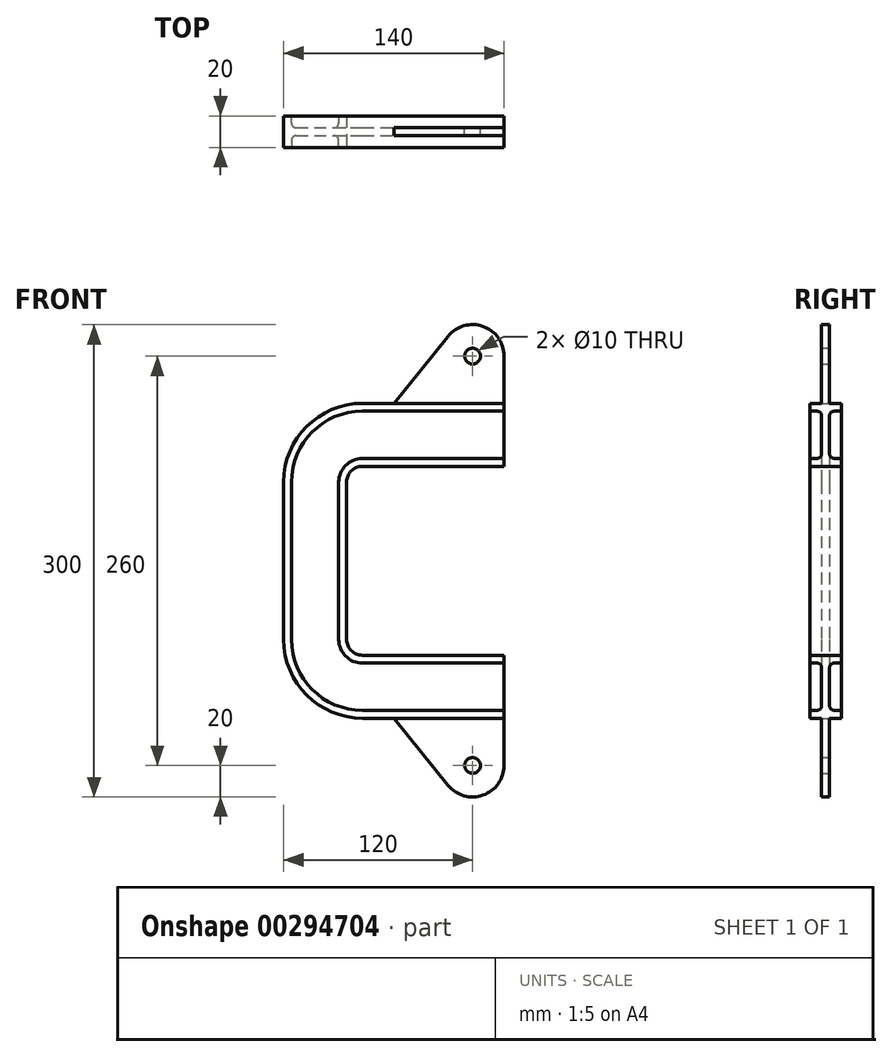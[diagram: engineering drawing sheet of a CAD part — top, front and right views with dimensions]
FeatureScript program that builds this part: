
annotation { "Feature Type Name" : "Feature", "Feature Type Description" : "" }
export const myFeature = defineFeature(function(context is Context, id is Id, definition is map)
    precondition{}
    {
        {
            var Q0;
            Q0=qCreatedBy(makeId("Front.planeOp"),FACE);
            var sketch = newSketch(context, id + "F0", { "sketchPlane" : qUnion([Q0])});
            skLineSegment(sketch, "E0", {"start": v(-100, 50) * mm, "end": v(-100, 0) * mm});
            skArc(sketch, "E1", {"start": v(-90, 60) * mm, "mid": v(-97.07, 57.07) * mm, "end": v(-100, 50) * mm});
            skLineSegment(sketch, "E2", {"start": v(-90, 60) * mm, "end": v(0, 60) * mm});
            skArc(sketch, "E3.MirrorCS", {"start": v(-90, -60) * mm, "mid": v(-97.07, -57.07) * mm, "end": v(-100, -50) * mm});
            skLineSegment(sketch, "E4.MirrorCS", {"start": v(-100, -50) * mm, "end": v(-100, 0) * mm});
            skLineSegment(sketch, "E5.MirrorCS", {"start": v(-90, -60) * mm, "end": v(0, -60) * mm});
            skSolve(sketch);
        }
        {
            var Q0;
            Q0=qCreatedBy(makeId("Right.planeOp"),FACE);
            var sketch = newSketch(context, id + "F1", { "sketchPlane" : qUnion([Q0])});
            skLineSegment(sketch, "E6", {"start": v(0, 60) * mm, "end": v(-10, 60) * mm});
            skLineSegment(sketch, "E7", {"start": v(-10, 60) * mm, "end": v(-10, 65) * mm});
            skLineSegment(sketch, "E8", {"start": v(-10, 65) * mm, "end": v(-5.5, 65) * mm});
            skArc(sketch, "E9", {"start": v(-5.5, 65) * mm, "mid": v(-3.38, 65.88) * mm, "end": v(-2.5, 68) * mm});
            skLineSegment(sketch, "E10", {"start": v(-2.5, 68) * mm, "end": v(-2.5, 92) * mm});
            skArc(sketch, "E11", {"start": v(-2.5, 92) * mm, "mid": v(-3.38, 94.12) * mm, "end": v(-5.5, 95) * mm});
            skLineSegment(sketch, "E12", {"start": v(-5.5, 95) * mm, "end": v(-10, 95) * mm});
            skLineSegment(sketch, "E13", {"start": v(-10, 95) * mm, "end": v(-10, 100) * mm});
            skLineSegment(sketch, "E14", {"start": v(-10, 100) * mm, "end": v(0, 100) * mm});
            skLineSegment(sketch, "E15.MirrorCS", {"start": v(5.5, 95) * mm, "end": v(10, 95) * mm});
            skLineSegment(sketch, "E16.MirrorCS", {"start": v(10, 65) * mm, "end": v(5.5, 65) * mm});
            skArc(sketch, "E17.MirrorCS", {"start": v(5.5, 65) * mm, "mid": v(3.38, 65.88) * mm, "end": v(2.5, 68) * mm});
            skLineSegment(sketch, "E18.MirrorCS", {"start": v(2.5, 68) * mm, "end": v(2.5, 92) * mm});
            skLineSegment(sketch, "E19.MirrorCS", {"start": v(10, 95) * mm, "end": v(10, 100) * mm});
            skLineSegment(sketch, "E20.MirrorCS", {"start": v(10, 100) * mm, "end": v(0, 100) * mm});
            skArc(sketch, "E21.MirrorCS", {"start": v(2.5, 92) * mm, "mid": v(3.38, 94.12) * mm, "end": v(5.5, 95) * mm});
            skLineSegment(sketch, "E22.MirrorCS", {"start": v(0, 60) * mm, "end": v(10, 60) * mm});
            skLineSegment(sketch, "E23.MirrorCS", {"start": v(10, 60) * mm, "end": v(10, 65) * mm});
            skSolve(sketch);
        }
        {
            var Q0;
            Q0=makeQuery(id+"F1.imprint","IMPRINT",FACE,{"disambiguationData":[TD([[makeQuery(id+"F1.imprint","IMPRINT",EDGE,{"derivedFrom":sQuery(id+"F1.wireOp",EDGE,"E6")}),-1.0]])]});
            var Q1;
            Q1=sQuery(id+"F0.wireOp",EDGE,"E2");
            var Q2;
            Q2=sQuery(id+"F0.wireOp",EDGE,"E1");
            var Q3;
            Q3=sQuery(id+"F0.wireOp",EDGE,"E0");
            var Q4;
            Q4=sQuery(id+"F0.wireOp",EDGE,"E4.MirrorCS");
            var Q5;
            Q5=sQuery(id+"F0.wireOp",EDGE,"E3.MirrorCS");
            var Q6;
            Q6=sQuery(id+"F0.wireOp",EDGE,"E5.MirrorCS");
            sweep(context, id + "F2", {"profiles" : qUnion([Q0]), "path" : qUnion([Q1, Q2, Q3, Q4, Q5, Q6])});
        }
        {
            var Q0;
            Q0=qCreatedBy(makeId("Front.planeOp"),FACE);
            var sketch = newSketch(context, id + "F3", { "sketchPlane" : qUnion([Q0])});
            skLineSegment(sketch, "E24", {"start": v(0, 100) * mm, "end": v(0, 130) * mm});
            skArc(sketch, "E25", {"start": v(0, 130) * mm, "mid": v(-13.33, 148.85) * mm, "end": v(-35.55, 142.58) * mm});
            skLineSegment(sketch, "E26", {"start": v(-35.55, 142.58) * mm, "end": v(-70, 100) * mm});
            skLineSegment(sketch, "E27", {"start": v(-70, 100) * mm, "end": v(0, 100) * mm});
            skCircle(sketch, "E28", {"center": v(-20, 130) * mm, "radius": 5 * mm});
            skSolve(sketch);
        }
        {
            var Q0;
            Q0=makeQuery(id+"F3.imprint","IMPRINT",FACE,{"disambiguationData":[TD([[makeQuery(id+"F3.imprint","IMPRINT",EDGE,{"derivedFrom":sQuery(id+"F3.wireOp",EDGE,"E24")}),1.0]])]});
            extrude(context, id + "F4", {"entities" : qUnion([Q0]), "operationType" : NewBodyOperationType.ADD, "endBound" : BoundingType.SYMMETRIC, "depth" : 5 * mm});
        }
        {
            var Q0;
            Q0=qCreatedBy(makeId("Front.planeOp"),FACE);
            var sketch = newSketch(context, id + "F5", { "sketchPlane" : qUnion([Q0])});
            skLineSegment(sketch, "E29", {"start": v(0, -100) * mm, "end": v(0, -130) * mm});
            skArc(sketch, "E30", {"start": v(-35.55, -142.58) * mm, "mid": v(-13.33, -148.85) * mm, "end": v(0, -130) * mm});
            skLineSegment(sketch, "E31", {"start": v(-35.55, -142.58) * mm, "end": v(-70, -100) * mm});
            skLineSegment(sketch, "E32", {"start": v(-70, -100) * mm, "end": v(0, -100) * mm});
            skCircle(sketch, "E33", {"center": v(-20, -130) * mm, "radius": 5 * mm});
            skSolve(sketch);
        }
        {
            var Q0;
            Q0=makeQuery(id+"F5.imprint","IMPRINT",FACE,{"disambiguationData":[TD([[makeQuery(id+"F5.imprint","IMPRINT",EDGE,{"derivedFrom":sQuery(id+"F5.wireOp",EDGE,"E29")}),-1.0]])]});
            extrude(context, id + "F6", {"entities" : qUnion([Q0]), "operationType" : NewBodyOperationType.ADD, "endBound" : BoundingType.SYMMETRIC, "depth" : 5 * mm});
        }
    });
